# Revit family: Domotics-DomesticRanges-GEWISS-CHORUS_CLIMATE-DAILY-WEEKLY_TIMER
name_source: partatom
category: Apparecchi elettrici
revit_build: Autodesk Revit 2016 (Build: 20161004_0715(x64)
units: mm (PartAtom-declared; Revit-internal decimal feet)

## family parameters
Condiviso = Sì
Host = Superficie
Mantenere orientamento annotazione = Sì
Punto di calcolo locali = Sì
Quota connettore circolare = Usa diametro
Taglio con vuoti quando caricato = Sì
Tipo di parte = Normale

## types (3) — shared parameters
Altezza_Termometro = 45 mm  [stored 0.147638 ft]
Catalogue = DOMOTICS
Catalogue Range = CHORUS - DOMESTIC RANGE
Description. = Programmer
Electrocod = 0141
IDF = 5ac071e2-b636-417d-aa84-081a2f27b228
IDT = c8a0c6df-912e-4acc-8e0a-20c261d53a2b
Immagine tipo = GW14581.jpg
Larghezza_Termometro = 23 mm  [stored 0.0754593 ft]
No. Chorus modules = 2
No. Chorus modules: = 2
Produttore = GEWISS S.p.A.
Prospetto di default = 1219 mm
SEO = Programmer
Supply voltage = 230 V ac - 50/60 Hz
Technical sheet = https://www.gewiss.com
Tipo_ = CHORUS PROGRAMMATORE_g : GW14581 Programmatore elettronico giornaliero/settimanale 2M titanio
URL = https://www.gewiss.com
Version file RFA = 19.0
finitura = GEWISS TITANIO

## per-type parameters (varying)
| type | Colour | Descrizione | EAN code | Modello |
| GW12581 - Dly/wkly electronic timer 1 channel 2M Black | Black | DLY/WKLY ELECTRONIC TIMER 1 CHANNEL 2M B | 8011564267374 | GW12581 |
| GW10581 - Dly/wkly electronic timer 1 channel 2M White | White | DLY/WKLY ELECTRONIC TIMER 1 CHANNEL 2M W | 8011564262973 | GW10581 |
| GW14581 - Dly/wkly electronic timer 1 channel 2M Titanium | Titanium | DLY/WKLY ELECTRONIC TIMER 1 CHANNEL 2M T | 8011564268029 | GW14581 |

note: [stored X ft] marks values corroborated as IEEE doubles in the binary element streams (Revit-internal decimal feet)

## geometry (parser evidence)
native form markers: Sweep x2
no freeform markers — native parametric forms only
